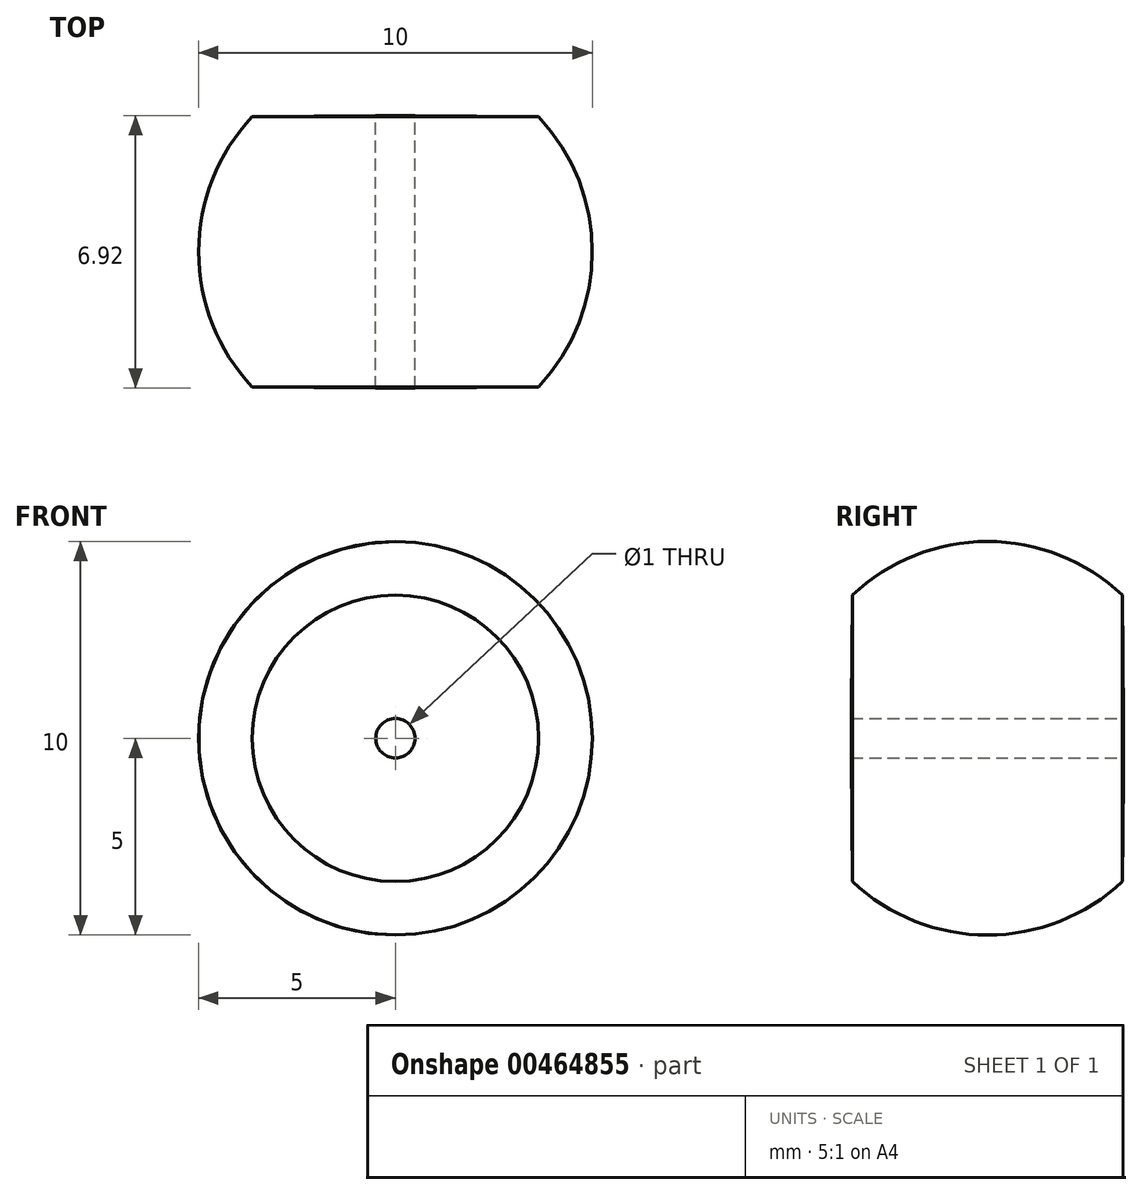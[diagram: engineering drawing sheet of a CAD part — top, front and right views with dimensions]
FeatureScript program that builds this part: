
annotation { "Feature Type Name" : "Feature", "Feature Type Description" : "" }
export const myFeature = defineFeature(function(context is Context, id is Id, definition is map)
    precondition{}
    {
        {
            var Q0;
            Q0=qCreatedBy(makeId("Front.planeOp"),FACE);
            var sketch = newSketch(context, id + "F0", { "sketchPlane" : qUnion([Q0])});
            skCircle(sketch, "E0", {"center": v(0, 0) * mm, "radius": 5 * mm});
            skLineSegment(sketch, "E1", {"start": v(0, 7.55) * mm, "end": v(0, -8.3) * mm});
            skSolve(sketch);
        }
        {
            var Q0;
            {var subQ0=sQuery(id+"F0.wireOp",EDGE,"E1");var subQ1=sQuery(id+"F0.wireOp",EDGE,"E0");var subQ2=makeQuery(id+"F0.imprint","INTERSECT",VERTEX,{"disambiguationData":[OD(0.0)],"derivedFrom":[subQ1,subQ0]});Q0=makeQuery(id+"F0.imprint","IMPRINT",FACE,{"disambiguationData":[TD([[makeQuery(id+"F0.imprint","IMPRINT",EDGE,{"disambiguationData":[TD([[subQ2,1.0]])],"derivedFrom":subQ1}),1.0]])]});}
            var Q1;
            Q1=sQuery(id+"F0.wireOp",EDGE,"E1");
            revolve(context, id + "F1", {"entities" : qUnion([Q0]), "axis" : qUnion([Q1]), "revolveType" : RevolveType.FULL});
        }
        {
            var Q0;
            Q0=sQuery(id+"F0.wireOp",VERTEX,"E0.center");
            var Q1;
            Q1=makeQuery(id+"F1.opRevolve","SWEPT_BODY",BODY,{"disambiguationData":[OSD([sQuery(id+"F0.wireOp",EDGE,"E0"),sQuery(id+"F0.wireOp",EDGE,"E1")])]});
            hole(context, id + "F2", {"style" : HoleStyle.SIMPLE, "endStyle" : HoleEndStyle.THROUGH, "oppositeDirection" : true, "holeDiameter" : 1 * mm, "isTappedThrough" : true, "tappedDepth" : 12 * mm, "tapClearance" : 3, "locations" : qUnion([Q0]), "scope" : qUnion([Q1])});
        }
        {
            var Q0;
            Q0=sQuery(id+"F0.wireOp",VERTEX,"E0.center");
            var Q1;
            Q1=makeQuery(id+"F1.opRevolve","SWEPT_BODY",BODY,{"disambiguationData":[OSD([sQuery(id+"F0.wireOp",EDGE,"E0"),sQuery(id+"F0.wireOp",EDGE,"E1")])]});
            hole(context, id + "F3", {"style" : HoleStyle.SIMPLE, "endStyle" : HoleEndStyle.THROUGH, "holeDiameter" : 1 * mm, "isTappedThrough" : true, "tappedDepth" : 12 * mm, "tapClearance" : 3, "locations" : qUnion([Q0]), "scope" : qUnion([Q1])});
        }
        {
            var Q0;
            Q0=makeQuery(id+"F2.hole-0.boolean.opBoolean","INTERSECT",EDGE,{"derivedFrom":[makeQuery(id+"F1.opRevolve","SWEPT_FACE",FACE,{"disambiguationData":[OSD([sQuery(id+"F0.wireOp",EDGE,"E0")])]}),makeQuery(id+"F2.hole-0.opRevolve","SWEPT_FACE",FACE,{"disambiguationData":[OSD([sQuery(id+"F2.hole-0.sketch.wireOp",EDGE,"core_line_2")])]})]});
            var Q1;
            Q1=makeQuery(id+"F1.opRevolve","SWEPT_FACE",FACE,{"disambiguationData":[OSD([sQuery(id+"F0.wireOp",EDGE,"E0")])]});
            chamfer(context, id + "F4", {"entities" : qUnion([Q0, Q1]), "chamferType" : ChamferType.OFFSET_ANGLE, "width" : 3.18 * mm, "oppositeDirection" : false, "angle" : 5 * degree, "tangentPropagation" : true});
        }
    });
